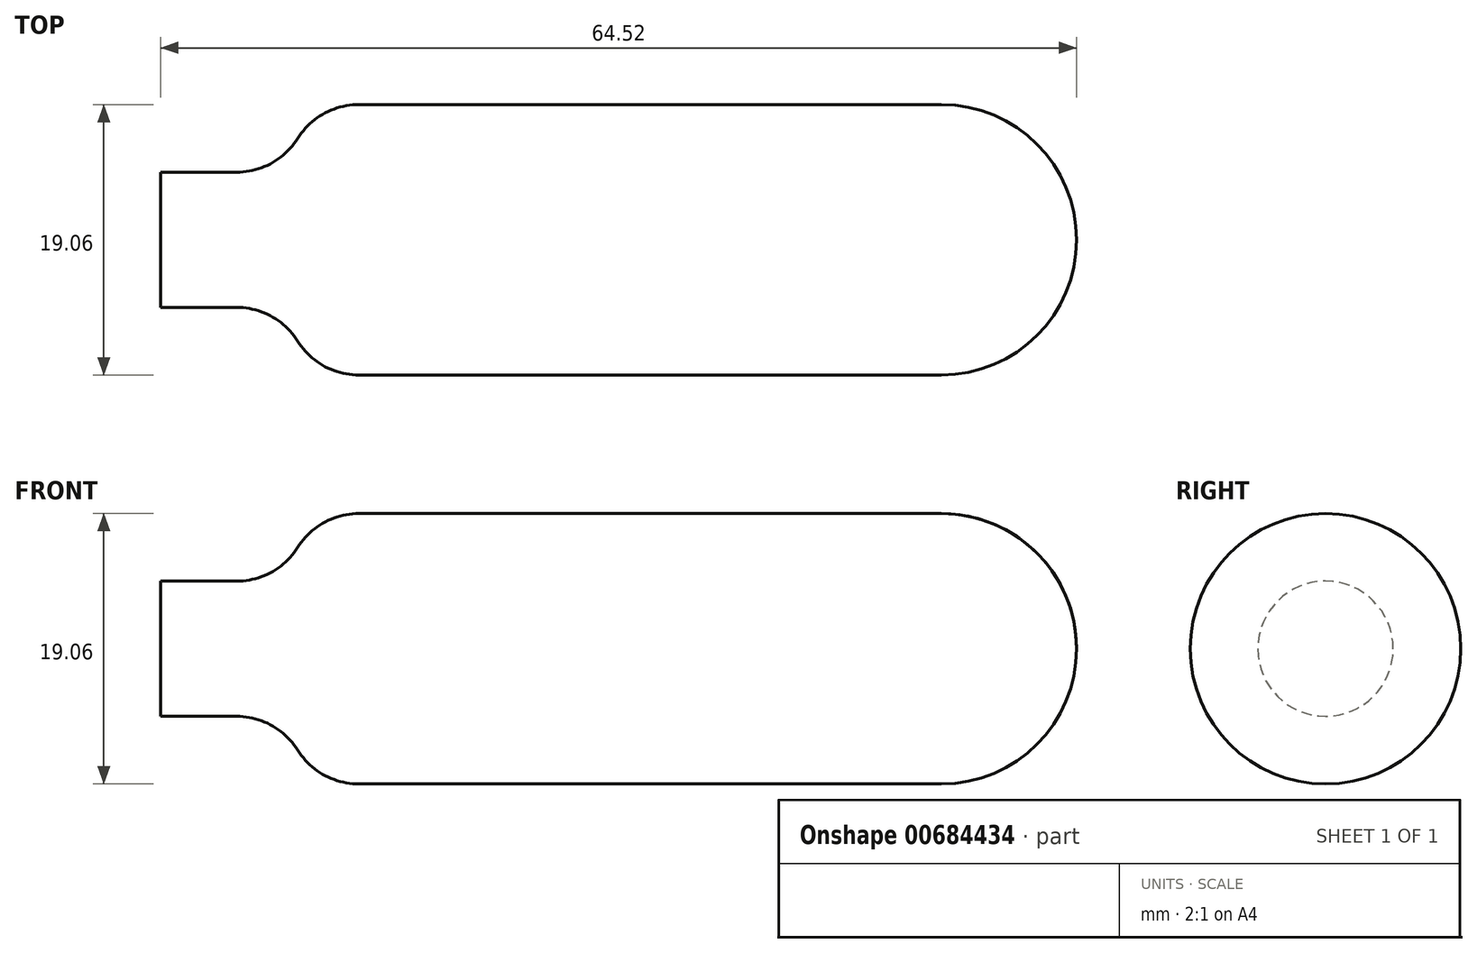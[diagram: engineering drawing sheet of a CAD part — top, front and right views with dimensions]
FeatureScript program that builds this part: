
annotation { "Feature Type Name" : "Feature", "Feature Type Description" : "" }
export const myFeature = defineFeature(function(context is Context, id is Id, definition is map)
    precondition{}
    {
        {
            var Q0;
            Q0=qCreatedBy(makeId("Front.planeOp"),FACE);
            var sketch = newSketch(context, id + "F0", { "sketchPlane" : qUnion([Q0])});
            skLineSegment(sketch, "E0", {"start": v(0, 0) * mm, "end": v(0, 4.76) * mm});
            skLineSegment(sketch, "E1", {"start": v(8.9, 9.53) * mm, "end": v(64.52, 9.53) * mm});
            skLineSegment(sketch, "E2", {"start": v(64.52, 9.53) * mm, "end": v(64.52, 0) * mm});
            skLineSegment(sketch, "E3", {"start": v(64.52, 0) * mm, "end": v(0, 0) * mm});
            skLineSegment(sketch, "E4", {"start": v(0, 4.76) * mm, "end": v(8.9, 4.76) * mm});
            skLineSegment(sketch, "E5", {"start": v(8.9, 4.76) * mm, "end": v(8.9, 9.53) * mm});
            skPoint(sketch, "E6.orphan", {"position": v(0, 9.53) * mm});
            skSolve(sketch);
        }
        {
            var Q0;
            Q0 = qSketchRegion(id + "F0", true);
            var Q1;
            Q1=sQuery(id+"F0.wireOp",EDGE,"E3");
            revolve(context, id + "F1", {"entities" : qUnion([Q0]), "axis" : qUnion([Q1]), "revolveType" : RevolveType.FULL});
        }
        {
            var Q0;
            Q0=makeQuery(id+"F1.opRevolve","SWEPT_EDGE",EDGE,{"disambiguationData":[OSD([sQuery(id+"F0.wireOp",EDGE,"E1"),sQuery(id+"F0.wireOp",EDGE,"E2")])]});
            fillet(context, id + "F2", {"entities" : qUnion([Q0]), "radius" : 9.52 * mm, "tangentPropagation" : true, "allowEdgeOverflow" : false});
        }
        {
            var Q0;
            Q0=makeQuery(id+"F1.opRevolve","SWEPT_EDGE",EDGE,{"disambiguationData":[OSD([sQuery(id+"F0.wireOp",EDGE,"E1"),sQuery(id+"F0.wireOp",EDGE,"E5")])]});
            fillet(context, id + "F3", {"entities" : qUnion([Q0]), "radius" : 5.08 * mm, "tangentPropagation" : true, "allowEdgeOverflow" : false});
        }
        {
            var Q0;
            Q0=makeQuery(id+"F3.opFillet","BLEND_EDGE",EDGE,{"blendedFrom":[makeQuery(id+"F1.opRevolve","SWEPT_EDGE",EDGE,{"disambiguationData":[OSD([sQuery(id+"F0.wireOp",EDGE,"E1"),sQuery(id+"F0.wireOp",EDGE,"E5")])]}),makeQuery(id+"F1.opRevolve","SWEPT_FACE",FACE,{"disambiguationData":[OSD([sQuery(id+"F0.wireOp",EDGE,"E4")])]})],"blendedInto":[makeQuery(id+"F1.opRevolve","SWEPT_FACE",FACE,{"disambiguationData":[OSD([sQuery(id+"F0.wireOp",EDGE,"E4")])]})]});
            fillet(context, id + "F4", {"entities" : qUnion([Q0]), "radius" : 5.08 * mm, "tangentPropagation" : true, "allowEdgeOverflow" : false});
        }
    });
